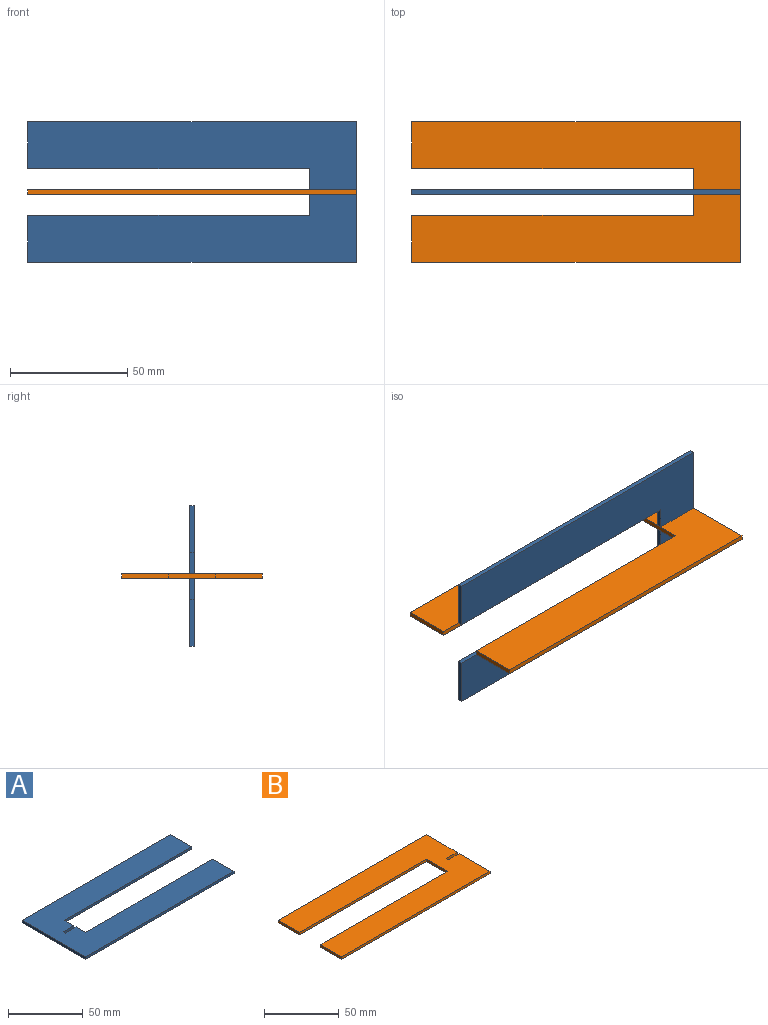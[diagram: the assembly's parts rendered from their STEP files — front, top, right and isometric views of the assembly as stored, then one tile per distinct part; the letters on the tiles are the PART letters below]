
ASSEMBLY  parts=2 mates=1
PART A: 14 faces, bbox 140x60x2 mm
  f0: plane 120x2mm, normal (0,-1,0), area 240mm2, adj f1,f11,f12,f13
  f1: plane 20x2mm, normal (1,0,0), area 40mm2, adj f0,f2,f12,f13
  f2: plane 140x2mm, normal (0,1,0), area 280mm2, adj f1,f3,f12,f13
  f3: plane 60x2mm, normal (-1,0,0), area 120mm2, adj f2,f4,f12,f13
  f4: plane 140x2mm, normal (0,-1,0), area 280mm2, adj f3,f5,f12,f13
  f5: plane 20x2mm, normal (1,0,0), area 40mm2, adj f4,f6,f12,f13
  f6: plane 120x2mm, normal (0,1,0), area 240mm2, adj f5,f7,f12,f13
  f7: plane 9x2mm, normal (1,0,0), area 18mm2, adj f6,f8,f12,f13
  f8: plane 10x2mm, normal (0,1,0), area 20mm2, adj f7,f9,f12,f13
  f9: plane 2x2mm, normal (1,0,0), area 4mm2, adj f8,f10,f12,f13
  f10: plane 10x2mm, normal (0,-1,0), area 20mm2, adj f9,f11,f12,f13
  f11: plane 9x2mm, normal (1,0,0), area 18mm2, adj f0,f10,f12,f13
  f12: plane 140x60mm, normal (0,0,1), area 5980mm2, adj f0,f1,f2,f3,f4,f5,f6,f7
  f13: plane 140x60mm, normal (0,0,-1), area 5980mm2, adj f0,f1,f2,f3,f4,f5,f6,f7
PART B: 14 faces, bbox 140x60x2 mm
  f0: plane 120x2mm, normal (0,-1,0), area 240mm2, adj f1,f11,f12,f13
  f1: plane 20x2mm, normal (-1,0,0), area 40mm2, adj f0,f2,f12,f13
  f2: plane 120x2mm, normal (0,1,0), area 240mm2, adj f1,f3,f12,f13
  f3: plane 20x2mm, normal (-1,0,0), area 40mm2, adj f2,f4,f12,f13
  f4: plane 140x2mm, normal (0,-1,0), area 280mm2, adj f3,f5,f12,f13
  f5: plane 29x2mm, normal (1,0,0), area 58mm2, adj f4,f6,f12,f13
  f6: plane 10x2mm, normal (0,1,0), area 20mm2, adj f5,f7,f12,f13
  f7: plane 2x2mm, normal (1,0,0), area 4mm2, adj f6,f8,f12,f13
  f8: plane 10x2mm, normal (0,-1,0), area 20mm2, adj f7,f9,f12,f13
  f9: plane 29x2mm, normal (1,0,0), area 58mm2, adj f8,f10,f12,f13
  f10: plane 140x2mm, normal (0,1,0), area 280mm2, adj f9,f11,f12,f13
  f11: plane 20x2mm, normal (-1,0,0), area 40mm2, adj f0,f10,f12,f13
  f12: plane 140x60mm, normal (0,0,1), area 5980mm2, adj f0,f1,f2,f3,f4,f5,f6,f7
  f13: plane 140x60mm, normal (0,0,-1), area 5980mm2, adj f0,f1,f2,f3,f4,f5,f6,f7
PLACE A rot(axis=(0,-0.71,-0.71),180deg) t=(-36.22,-35.15,-14.85)mm
PLACE B t=(-36.22,-24.15,-5.85)mm
MATE fastened A.f9 <-> B.f7  axis (-1,0,0) through (33.78,-34.15,-4.85)mm
